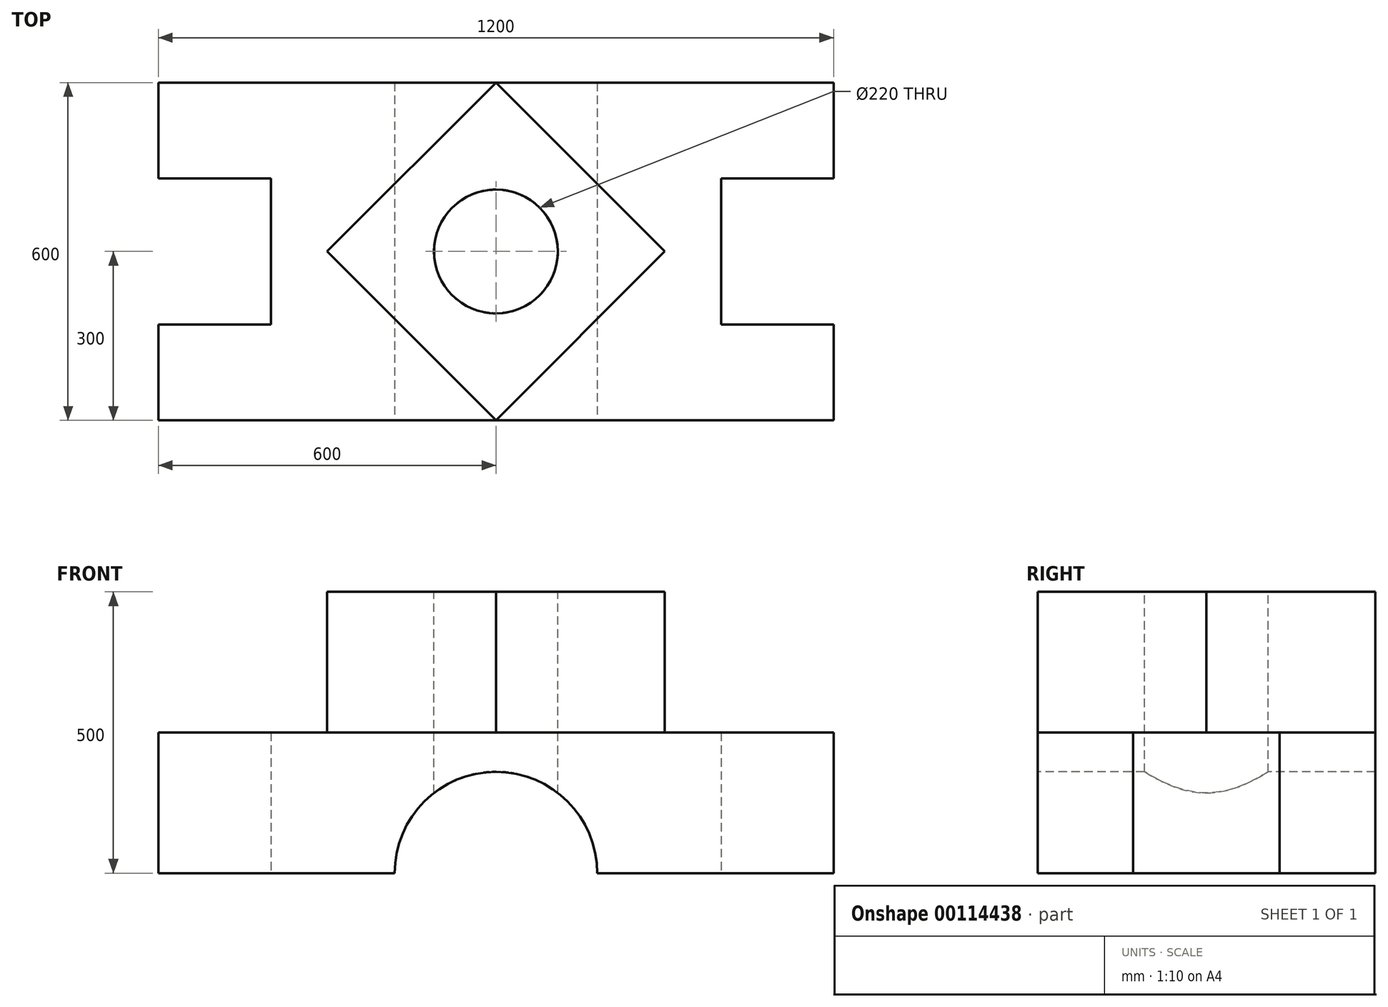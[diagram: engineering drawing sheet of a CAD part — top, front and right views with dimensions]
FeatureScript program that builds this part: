
annotation { "Feature Type Name" : "Feature", "Feature Type Description" : "" }
export const myFeature = defineFeature(function(context is Context, id is Id, definition is map)
    precondition{}
    {
        {
            var Q0;
            Q0=qCreatedBy(makeId("Top.planeOp"),FACE);
            var sketch = newSketch(context, id + "F0", { "sketchPlane" : qUnion([Q0])});
            skLineSegment(sketch, "E0.bottom", {"start": v(-600, 300) * mm, "end": v(600, 300) * mm});
            skLineSegment(sketch, "E0.top", {"start": v(-600, -300) * mm, "end": v(600, -300) * mm});
            skLineSegment(sketch, "E0.left", {"start": v(-600, 300) * mm, "end": v(-600, 130) * mm});
            skLineSegment(sketch, "E0.right", {"start": v(600, 300) * mm, "end": v(600, 130) * mm});
            skPoint(sketch, "E0.middle", {"position": v(0, 0) * mm});
            skLineSegment(sketch, "E1.top", {"start": v(-600, 130) * mm, "end": v(-400, 130) * mm});
            skLineSegment(sketch, "E1.right", {"start": v(-400, -130) * mm, "end": v(-400, 130) * mm});
            skPoint(sketch, "E1.middle", {"position": v(-600, 0) * mm});
            skLineSegment(sketch, "E2.bottom", {"start": v(600, 130) * mm, "end": v(400, 130) * mm});
            skLineSegment(sketch, "E2.top", {"start": v(600, -130) * mm, "end": v(400, -130) * mm});
            skLineSegment(sketch, "E2.right", {"start": v(400, 130) * mm, "end": v(400, -130) * mm});
            skPoint(sketch, "E2.middle", {"position": v(600, 0) * mm});
            skLineSegment(sketch, "E3.trimOffspring", {"start": v(600, -130) * mm, "end": v(600, -300) * mm});
            skPoint(sketch, "E4.orphan", {"position": v(800, -130) * mm});
            skPoint(sketch, "E5.orphan", {"position": v(800, 130) * mm});
            skPoint(sketch, "E1.left.end.orphan", {"position": v(-800, 130) * mm});
            skPoint(sketch, "E6.orphan", {"position": v(-800, -130) * mm});
            skLineSegment(sketch, "E7", {"start": v(-400, -130) * mm, "end": v(-600, -130) * mm});
            skLineSegment(sketch, "E8.trimOffspring", {"start": v(-600, -130) * mm, "end": v(-600, -300) * mm});
            skSolve(sketch);
        }
        {
            var Q0;
            Q0 = qSketchRegion(id + "F0", true);
            extrude(context, id + "F1", {"entities" : qUnion([Q0]), "depth" : 250 * mm});
        }
        {
            var Q0;
            Q0=makeQuery(id+"F1.opExtrude","SWEPT_FACE",FACE,{"disambiguationData":[OSD([sQuery(id+"F0.wireOp",EDGE,"E0.top")])]});
            var sketch = newSketch(context, id + "F2", { "sketchPlane" : qUnion([Q0])});
            skCircle(sketch, "E9", {"center": v(0, 0) * mm, "radius": 180 * mm});
            skSolve(sketch);
        }
        {
            var Q0;
            Q0 = qSketchRegion(id + "F2", true);
            extrude(context, id + "F3", {"entities" : qUnion([Q0]), "operationType" : NewBodyOperationType.REMOVE, "endBound" : BoundingType.THROUGH_ALL, "oppositeDirection" : true, "depth" : 25 * mm});
        }
        {
            var Q0;
            Q0=makeQuery(id+"F1.opExtrude","CAP_FACE",FACE,{"disambiguationData":[OSD([sQuery(id+"F0.wireOp",EDGE,"E0.bottom"),sQuery(id+"F0.wireOp",EDGE,"E0.top"),sQuery(id+"F0.wireOp",EDGE,"E0.left"),sQuery(id+"F0.wireOp",EDGE,"E0.right"),sQuery(id+"F0.wireOp",EDGE,"E1.top"),sQuery(id+"F0.wireOp",EDGE,"E1.right"),sQuery(id+"F0.wireOp",EDGE,"E2.bottom"),sQuery(id+"F0.wireOp",EDGE,"E2.top"),sQuery(id+"F0.wireOp",EDGE,"E2.right"),sQuery(id+"F0.wireOp",EDGE,"E3.trimOffspring"),sQuery(id+"F0.wireOp",EDGE,"E7"),sQuery(id+"F0.wireOp",EDGE,"E8.trimOffspring")])],"isStart":false});
            var sketch = newSketch(context, id + "F4", { "sketchPlane" : qUnion([Q0])});
            skCircle(sketch, "E10.cCircle", {"center": v(0, 0) * mm, "radius": 212.13 * mm, "construction": true});
            skLineSegment(sketch, "E10.0", {"start": v(0, 300) * mm, "end": v(300, 0) * mm});
            skLineSegment(sketch, "E10.1", {"start": v(300, 0) * mm, "end": v(0, -300) * mm});
            skLineSegment(sketch, "E10.2", {"start": v(0, -300) * mm, "end": v(-300, 0) * mm});
            skLineSegment(sketch, "E10.3", {"start": v(-300, 0) * mm, "end": v(0, 300) * mm});
            skPoint(sketch, "E10.0.midPoint", {"position": v(150, 150) * mm});
            skSolve(sketch);
        }
        {
            var Q0;
            Q0 = qSketchRegion(id + "F4", true);
            extrude(context, id + "F5", {"entities" : qUnion([Q0]), "operationType" : NewBodyOperationType.ADD, "depth" : 250 * mm});
        }
        {
            var Q0;
            Q0=makeQuery(id+"F5.opExtrude","CAP_FACE",FACE,{"disambiguationData":[OSD([sQuery(id+"F4.wireOp",EDGE,"E10.0"),sQuery(id+"F4.wireOp",EDGE,"E10.1"),sQuery(id+"F4.wireOp",EDGE,"E10.2"),sQuery(id+"F4.wireOp",EDGE,"E10.3")])],"isStart":false});
            var sketch = newSketch(context, id + "F6", { "sketchPlane" : qUnion([Q0])});
            skCircle(sketch, "E11", {"center": v(0, 0) * mm, "radius": 110 * mm});
            skSolve(sketch);
        }
        {
            var Q0;
            Q0 = qSketchRegion(id + "F6", true);
            extrude(context, id + "F7", {"entities" : qUnion([Q0]), "operationType" : NewBodyOperationType.REMOVE, "endBound" : BoundingType.THROUGH_ALL, "oppositeDirection" : true, "depth" : 25 * mm});
        }
    });
